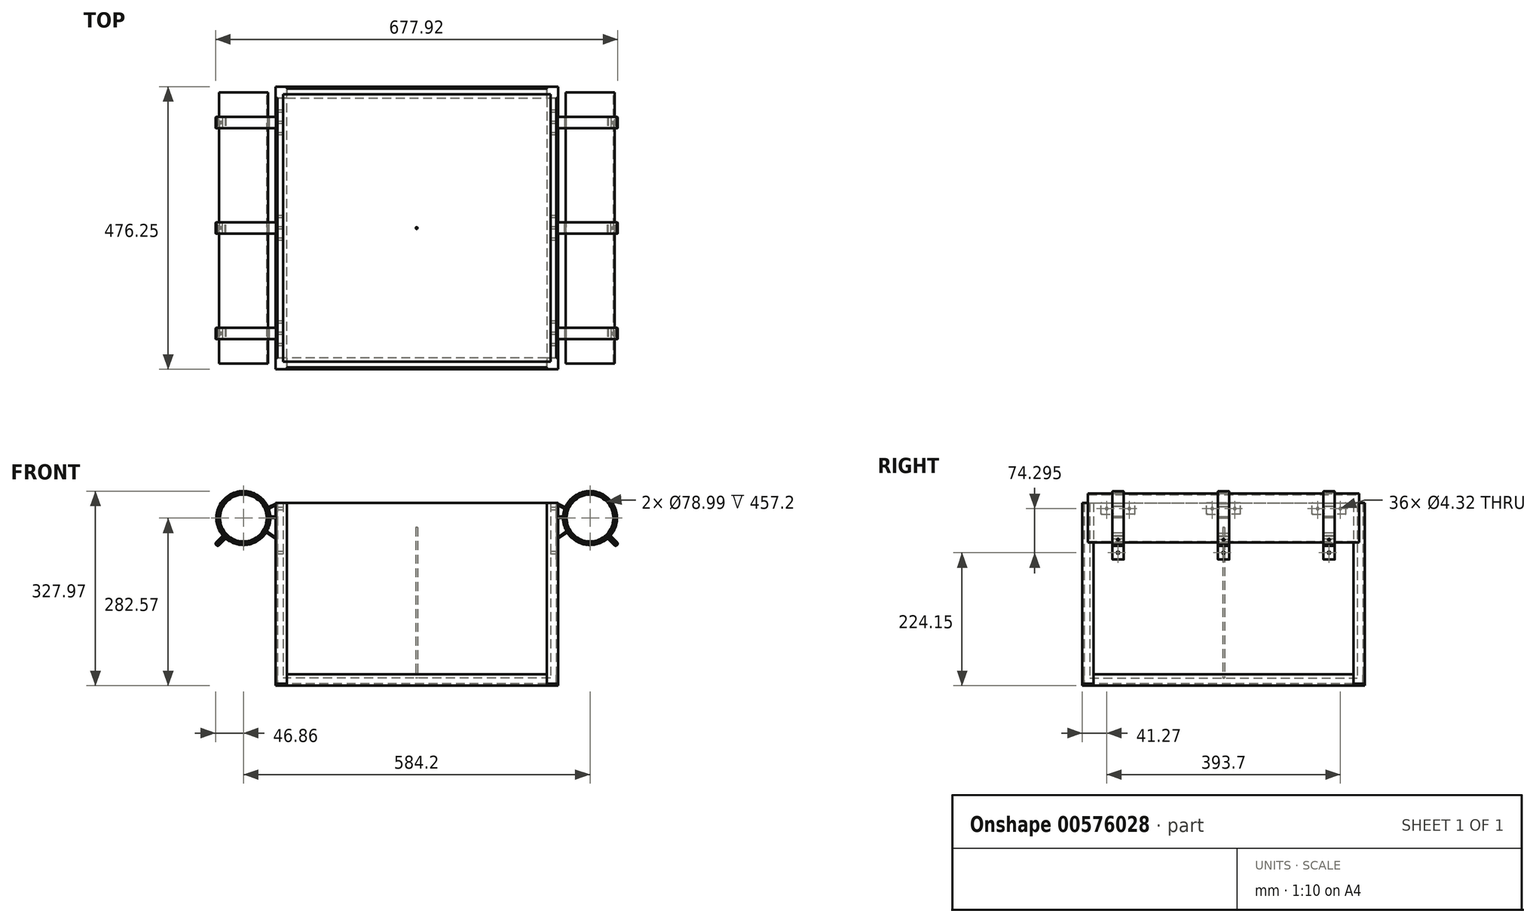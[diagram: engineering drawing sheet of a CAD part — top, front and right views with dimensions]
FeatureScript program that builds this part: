
annotation { "Feature Type Name" : "Feature", "Feature Type Description" : "" }
export const myFeature = defineFeature(function(context is Context, id is Id, definition is map)
    precondition{}
    {
        {
            var Q0;
            Q0=qCreatedBy(makeId("Top.planeOp"),FACE);
            var sketch = newSketch(context, id + "F0", { "sketchPlane" : qUnion([Q0])});
            skLineSegment(sketch, "E0.bottom", {"start": v(234.95, -234.95) * mm, "end": v(-234.95, -234.95) * mm});
            skLineSegment(sketch, "E0.top", {"start": v(234.95, 234.95) * mm, "end": v(-234.95, 234.95) * mm});
            skLineSegment(sketch, "E0.left", {"start": v(234.95, -234.95) * mm, "end": v(234.95, 234.95) * mm});
            skLineSegment(sketch, "E0.right", {"start": v(-234.95, -234.95) * mm, "end": v(-234.95, 234.95) * mm});
            skPoint(sketch, "E0.middle", {"position": v(0, 0) * mm});
            skLineSegment(sketch, "E1", {"start": v(-234.95, 238.13) * mm, "end": v(-238.13, 238.13) * mm});
            skLineSegment(sketch, "E2", {"start": v(-238.13, 238.13) * mm, "end": v(-238.13, 219.08) * mm});
            skLineSegment(sketch, "E3", {"start": v(-238.13, 219.08) * mm, "end": v(-234.95, 219.08) * mm});
            skLineSegment(sketch, "E4", {"start": v(-238.13, 238.13) * mm, "end": v(-219.08, 238.13) * mm});
            skLineSegment(sketch, "E5", {"start": v(-219.08, 238.13) * mm, "end": v(-219.08, 234.95) * mm});
            skLineSegment(sketch, "E6.1.0", {"start": v(-238.13, -238.13) * mm, "end": v(-238.13, -219.08) * mm});
            skLineSegment(sketch, "E6.1.1", {"start": v(-238.13, -238.13) * mm, "end": v(-219.08, -238.13) * mm});
            skLineSegment(sketch, "E6.1.2", {"start": v(-219.08, -238.13) * mm, "end": v(-219.08, -234.95) * mm});
            skLineSegment(sketch, "E6.1.3", {"start": v(-238.13, -219.08) * mm, "end": v(-234.95, -219.08) * mm});
            skLineSegment(sketch, "E6.1.4", {"start": v(-238.13, -234.95) * mm, "end": v(-238.13, -238.13) * mm});
            skLineSegment(sketch, "E6.2.0", {"start": v(238.13, -238.13) * mm, "end": v(219.08, -238.13) * mm});
            skLineSegment(sketch, "E6.2.1", {"start": v(238.13, -238.13) * mm, "end": v(238.13, -219.08) * mm});
            skLineSegment(sketch, "E6.2.2", {"start": v(238.13, -219.08) * mm, "end": v(234.95, -219.08) * mm});
            skLineSegment(sketch, "E6.2.3", {"start": v(219.08, -238.13) * mm, "end": v(219.08, -234.95) * mm});
            skLineSegment(sketch, "E6.2.4", {"start": v(234.95, -238.13) * mm, "end": v(238.13, -238.13) * mm});
            skLineSegment(sketch, "E6.3.0", {"start": v(238.13, 238.13) * mm, "end": v(238.13, 219.08) * mm});
            skLineSegment(sketch, "E6.3.1", {"start": v(238.13, 238.13) * mm, "end": v(219.08, 238.13) * mm});
            skLineSegment(sketch, "E6.3.2", {"start": v(219.08, 238.13) * mm, "end": v(219.08, 234.95) * mm});
            skLineSegment(sketch, "E6.3.3", {"start": v(238.13, 219.08) * mm, "end": v(234.95, 219.08) * mm});
            skLineSegment(sketch, "E6.3.4", {"start": v(238.13, 234.95) * mm, "end": v(238.13, 238.13) * mm});
            skLineSegment(sketch, "E7.0", {"start": v(225.43, 225.43) * mm, "end": v(-225.42, 225.42) * mm});
            skLineSegment(sketch, "E7.1", {"start": v(225.43, -225.42) * mm, "end": v(225.43, 225.42) * mm});
            skLineSegment(sketch, "E7.2", {"start": v(225.43, -225.42) * mm, "end": v(-225.43, -225.43) * mm});
            skLineSegment(sketch, "E7.3", {"start": v(-225.43, -225.43) * mm, "end": v(-225.42, 225.42) * mm});
            skSolve(sketch);
        }
        {
            var Q0;
            Q0=qSketchRegion(id+"F0",true);
            extrude(context, id + "F1", {"entities" : qUnion([Q0]), "depth" : 304.8 * mm, "offsetDistance" : 25.4 * mm});
        }
        {
            var Q0;
            Q0=makeQuery(id+"F0.imprint","IMPRINT",FACE,{"disambiguationData":[TD([[makeQuery(id+"F0.imprint","IMPRINT",EDGE,{"derivedFrom":sQuery(id+"F0.wireOp",EDGE,"E7.0")}),1.0]])]});
            extrude(context, id + "F2", {"entities" : qUnion([Q0]), "operationType" : NewBodyOperationType.ADD, "depth" : 9.52 * mm, "offsetDistance" : 25.4 * mm});
        }
        {
            var Q0;
            Q0=makeQuery(id+"F1.opExtrude","SWEPT_FACE",FACE,{"disambiguationData":[OSD([sQuery(id+"F0.wireOp",EDGE,"E0.right")])]});
            var sketch = newSketch(context, id + "F3", { "sketchPlane" : qUnion([Q0])});
            skLineSegment(sketch, "E8", {"start": v(0, 304.8) * mm, "end": v(0, 297.18) * mm});
            skLineSegment(sketch, "E9", {"start": v(0, 304.8) * mm, "end": v(-177.8, 304.8) * mm});
            skLineSegment(sketch, "E10", {"start": v(-177.8, 304.8) * mm, "end": v(-177.8, 297.18) * mm});
            skLineSegment(sketch, "E11", {"start": v(0, 297.18) * mm, "end": v(0, 220.98) * mm});
            skLineSegment(sketch, "E12", {"start": v(-177.8, 297.18) * mm, "end": v(-177.8, 220.98) * mm});
            skLineSegment(sketch, "E13.MirrorCS", {"start": v(177.8, 304.8) * mm, "end": v(177.8, 297.18) * mm});
            skLineSegment(sketch, "E14.MirrorCS", {"start": v(177.8, 297.18) * mm, "end": v(177.8, 220.98) * mm});
            skLineSegment(sketch, "E15.MirrorCS", {"start": v(0, 304.8) * mm, "end": v(177.8, 304.8) * mm});
            skLineSegment(sketch, "E16", {"start": v(-177.8, 304.8) * mm, "end": v(-177.8, 295.28) * mm});
            skLineSegment(sketch, "E17", {"start": v(-177.8, 295.28) * mm, "end": v(-158.75, 295.28) * mm});
            skLineSegment(sketch, "E18.MirrorCS", {"start": v(-177.8, 295.28) * mm, "end": v(-196.85, 295.28) * mm});
            skLineSegment(sketch, "E19", {"start": v(-88.9, 304.8) * mm, "end": v(-88.9, 246.4) * mm});
            skLineSegment(sketch, "E20.MirrorCS", {"start": v(0, 304.8) * mm, "end": v(0, 295.28) * mm});
            skLineSegment(sketch, "E21.MirrorCS", {"start": v(0, 295.28) * mm, "end": v(19.05, 295.28) * mm});
            skLineSegment(sketch, "E22.MirrorCS", {"start": v(0, 295.28) * mm, "end": v(-19.05, 295.28) * mm});
            skLineSegment(sketch, "E23.MirrorCS", {"start": v(177.8, 304.8) * mm, "end": v(177.8, 295.28) * mm});
            skLineSegment(sketch, "E24.MirrorCS", {"start": v(177.8, 295.28) * mm, "end": v(196.85, 295.28) * mm});
            skLineSegment(sketch, "E25.MirrorCS", {"start": v(177.8, 295.28) * mm, "end": v(158.75, 295.28) * mm});
            skSolve(sketch);
        }
        {
            var Q0;
            Q0=sQuery(id+"F3.wireOp",VERTEX,"E11.end");
            var Q1;
            Q1=sQuery(id+"F3.wireOp",VERTEX,"E14.MirrorCS.end");
            var Q2;
            Q2=sQuery(id+"F3.wireOp",VERTEX,"E17.end");
            var Q3;
            Q3=sQuery(id+"F3.wireOp",VERTEX,"E18.MirrorCS.end");
            var Q4;
            Q4=sQuery(id+"F3.wireOp",VERTEX,"E22.MirrorCS.end");
            var Q5;
            Q5=sQuery(id+"F3.wireOp",VERTEX,"E21.MirrorCS.end");
            var Q6;
            Q6=sQuery(id+"F3.wireOp",VERTEX,"E12.end");
            var Q7;
            Q7=sQuery(id+"F3.wireOp",VERTEX,"E24.MirrorCS.end");
            var Q8;
            Q8=sQuery(id+"F3.wireOp",VERTEX,"E25.MirrorCS.end");
            var Q9;
            Q9=makeQuery(id+"F1.opExtrude","SWEPT_BODY",BODY,{"disambiguationData":[OSD([sQuery(id+"F0.wireOp",EDGE,"E0.bottom"),sQuery(id+"F0.wireOp",EDGE,"E0.top"),sQuery(id+"F0.wireOp",EDGE,"E0.left"),sQuery(id+"F0.wireOp",EDGE,"E0.right"),sQuery(id+"F0.wireOp",EDGE,"E2"),sQuery(id+"F0.wireOp",EDGE,"E3"),sQuery(id+"F0.wireOp",EDGE,"E4"),sQuery(id+"F0.wireOp",EDGE,"E5"),sQuery(id+"F0.wireOp",EDGE,"E6.1.0"),sQuery(id+"F0.wireOp",EDGE,"E6.1.1"),sQuery(id+"F0.wireOp",EDGE,"E6.1.2"),sQuery(id+"F0.wireOp",EDGE,"E6.1.3"),sQuery(id+"F0.wireOp",EDGE,"E6.1.4"),sQuery(id+"F0.wireOp",EDGE,"E6.2.0"),sQuery(id+"F0.wireOp",EDGE,"E6.2.1"),sQuery(id+"F0.wireOp",EDGE,"E6.2.2"),sQuery(id+"F0.wireOp",EDGE,"E6.2.3"),sQuery(id+"F0.wireOp",EDGE,"E6.2.4"),sQuery(id+"F0.wireOp",EDGE,"E6.3.0"),sQuery(id+"F0.wireOp",EDGE,"E6.3.1"),sQuery(id+"F0.wireOp",EDGE,"E6.3.2"),sQuery(id+"F0.wireOp",EDGE,"E6.3.3"),sQuery(id+"F0.wireOp",EDGE,"E6.3.4"),sQuery(id+"F0.wireOp",EDGE,"E7.0"),sQuery(id+"F0.wireOp",EDGE,"E7.1"),sQuery(id+"F0.wireOp",EDGE,"E7.2"),sQuery(id+"F0.wireOp",EDGE,"E7.3")])]});
            hole(context, id + "F4", {"style" : HoleStyle.SIMPLE, "endStyle" : HoleEndStyle.BLIND, "standardTappedOrClearance" : lookupTablePath({ "standard" : "ANSI", "fit" : "Close", "size" : "#8", "type" : "Clearance" }), "standardBlindInLast" : lookupTablePath({ "fit" : "Close", "standard" : "ANSI", "size" : "#8", "type" : "Clearance" }), "holeDiameter" : 4.32 * mm, "holeDepth" : 762 * mm, "isTappedThrough" : true, "tappedDepth" : 12.7 * mm, "tapClearance" : 3, "locations" : qUnion([Q0, Q1, Q2, Q3, Q4, Q5, Q6, Q7, Q8]), "scope" : qUnion([Q9]), "majorDiameter" : 6.35 * mm});
        }
        {
            var Q0;
            Q0=makeQuery(id+"F1.opExtrude","SWEPT_FACE",FACE,{"disambiguationData":[OSD([sQuery(id+"F0.wireOp",EDGE,"E6.1.2")])]});
            var sketch = newSketch(context, id + "F5", { "sketchPlane" : qUnion([Q0])});
            skLineSegment(sketch, "E26", {"start": v(-238.12, -3.17) * mm, "end": v(-238.12, 15.87) * mm});
            skLineSegment(sketch, "E27", {"start": v(-238.12, 15.87) * mm, "end": v(-234.95, 15.87) * mm});
            skLineSegment(sketch, "E28", {"start": v(-234.95, 15.87) * mm, "end": v(-234.95, 0) * mm});
            skLineSegment(sketch, "E29", {"start": v(-234.95, 0) * mm, "end": v(-219.07, 0) * mm});
            skLineSegment(sketch, "E30", {"start": v(-219.07, 0) * mm, "end": v(-219.07, -3.17) * mm});
            skLineSegment(sketch, "E31", {"start": v(-219.07, -3.17) * mm, "end": v(-238.12, -3.17) * mm});
            skSolve(sketch);
        }
        {
            var Q0;
            Q0=qSketchRegion(id+"F5",true);
            var Q1;
            Q1=makeQuery(id+"F1.opExtrude","SWEPT_FACE",FACE,{"disambiguationData":[OSD([sQuery(id+"F0.wireOp",EDGE,"E6.2.3")])]});
            extrude(context, id + "F6", {"entities" : qUnion([Q0]), "endBound" : BoundingType.UP_TO_SURFACE, "depth" : 25.4 * mm, "endBoundEntityFace" : qUnion([Q1]), "offsetDistance" : 25.4 * mm});
        }
        {
            var Q0;
            Q0=makeQuery(id+"F2.opExtrude","CAP_FACE",FACE,{"disambiguationData":[OSD([sQuery(id+"F0.wireOp",EDGE,"E7.0"),sQuery(id+"F0.wireOp",EDGE,"E7.1"),sQuery(id+"F0.wireOp",EDGE,"E7.2"),sQuery(id+"F0.wireOp",EDGE,"E7.3")])],"isStart":false});
            var sketch = newSketch(context, id + "F7", { "sketchPlane" : qUnion([Q0])});
            skCircle(sketch, "E32", {"center": v(0, 0) * mm, "radius": 1.59 * mm});
            skSolve(sketch);
        }
        {
            var Q0;
            Q0=qSketchRegion(id+"F7",true);
            extrude(context, id + "F8", {"entities" : qUnion([Q0]), "operationType" : NewBodyOperationType.ADD, "depth" : 254 * mm, "offsetDistance" : 25.4 * mm});
        }
        {
            var Q0;
            Q0=makeQuery(id+"F6.opExtrude","SWEPT_BODY",BODY,{"disambiguationData":[OSD([sQuery(id+"F5.wireOp",EDGE,"E26"),sQuery(id+"F5.wireOp",EDGE,"E27"),sQuery(id+"F5.wireOp",EDGE,"E28"),sQuery(id+"F5.wireOp",EDGE,"E29"),sQuery(id+"F5.wireOp",EDGE,"E30"),sQuery(id+"F5.wireOp",EDGE,"E31")])]});
            var Q1;
            Q1=makeQuery(id+"F8.opExtrude","SWEPT_FACE",FACE,{"disambiguationData":[OSD([sQuery(id+"F7.wireOp",EDGE,"E32")])]});
            circularPattern(context, id + "F9", {"entities" : qUnion([Q0]), "axis" : qUnion([Q1]), "angle" : 360 * degree, "instanceCount" : 4, "equalSpace" : true});
        }
        {
            var Q0;
            Q0=qCreatedBy(makeId("Front.planeOp"),FACE);
            var sketch = newSketch(context, id + "F10", { "sketchPlane" : qUnion([Q0])});
            skLineSegment(sketch, "E33", {"start": v(0, 0) * mm, "end": v(0, 279.4) * mm});
            skLineSegment(sketch, "E34", {"start": v(0, 279.4) * mm, "end": v(238.13, 279.4) * mm});
            skCircle(sketch, "E35", {"center": v(292.1, 279.4) * mm, "radius": 41.28 * mm});
            skCircle(sketch, "E36", {"center": v(292.1, 279.4) * mm, "radius": 39.5 * mm});
            skLineSegment(sketch, "E37", {"start": v(292.1, 279.4) * mm, "end": v(250.83, 279.4) * mm});
            skLineSegment(sketch, "E38", {"start": v(250.83, 279.4) * mm, "end": v(238.13, 279.4) * mm});
            skSolve(sketch);
        }
        {
            var Q0;
            Q0 = qSketchRegion(id + "F10", true);
            extrude(context, id + "F11", {"entities" : qUnion([Q0]), "endBound" : BoundingType.SYMMETRIC, "depth" : 457.2 * mm, "offsetDistance" : 25.4 * mm});
        }
        {
            var Q0;
            Q0=qCreatedBy(makeId("Front.planeOp"),FACE);
            var sketch = newSketch(context, id + "F12", { "sketchPlane" : qUnion([Q0])});
            skLineSegment(sketch, "E39", {"start": v(0, 0) * mm, "end": v(0, 40.83) * mm});
            skLineSegment(sketch, "E40", {"start": v(248.33, 298.8) * mm, "end": v(237.5, 303.6) * mm});
            skLineSegment(sketch, "E41", {"start": v(237.5, 209.55) * mm, "end": v(234.95, 209.55) * mm});
            skLineSegment(sketch, "E42", {"start": v(251.7, 253.53) * mm, "end": v(238.58, 244.41) * mm});
            skArc(sketch, "E43.0", {"start": v(322.94, 249.64) * mm, "mid": v(261.8, 309.7) * mm, "end": v(321.86, 248.56) * mm});
            skArc(sketch, "E44.0", {"start": v(246.75, 277.28) * mm, "mid": v(248.16, 267.95) * mm, "end": v(251.48, 259.12) * mm});
            skLineSegment(sketch, "E45", {"start": v(244.2, 279.7) * mm, "end": v(240.03, 279.7) * mm});
            skLineSegment(sketch, "E46.0", {"start": v(244.46, 282.24) * mm, "end": v(240.03, 282.24) * mm});
            skLineSegment(sketch, "E47.trimOffspring", {"start": v(237.5, 296.8) * mm, "end": v(237.5, 284.78) * mm});
            skLineSegment(sketch, "E48.trimOffspring", {"start": v(247.46, 296.1) * mm, "end": v(241.11, 299.1) * mm});
            skLineSegment(sketch, "E49.trimOffspring", {"start": v(237.5, 277.16) * mm, "end": v(237.5, 251.6) * mm});
            skArc(sketch, "E50.trimOffspring", {"start": v(255.22, 252.93) * mm, "mid": v(285.65, 234.46) * mm, "end": v(320.05, 243.62) * mm});
            skLineSegment(sketch, "E51.trimOffspring", {"start": v(250.66, 255.9) * mm, "end": v(241.48, 249.52) * mm});
            skLineSegment(sketch, "E52.trimOffspring", {"start": v(237.5, 242.33) * mm, "end": v(237.5, 209.55) * mm});
            skArc(sketch, "E53.trimOffspring", {"start": v(248.8, 293.05) * mm, "mid": v(247.68, 288.82) * mm, "end": v(246.98, 284.5) * mm});
            skLineSegment(sketch, "E54", {"start": v(292.1, 279.4) * mm, "end": v(292.1, 252.05) * mm});
            skLineSegment(sketch, "E55", {"start": v(292.1, 279.4) * mm, "end": v(324.2, 247.3) * mm});
            skLineSegment(sketch, "E56", {"start": v(324.2, 247.3) * mm, "end": v(337.67, 233.83) * mm});
            skLineSegment(sketch, "E57.0", {"start": v(323.66, 246.76) * mm, "end": v(337.14, 233.28) * mm});
            skLineSegment(sketch, "E58.0", {"start": v(324.74, 247.84) * mm, "end": v(338.22, 234.36) * mm});
            skArc(sketch, "E59.trimOffspring", {"start": v(327.88, 251.45) * mm, "mid": v(316.48, 317.7) * mm, "end": v(251.62, 299.97) * mm});
            skLineSegment(sketch, "E60", {"start": v(323.66, 246.76) * mm, "end": v(321.86, 248.56) * mm});
            skLineSegment(sketch, "E61", {"start": v(324.74, 247.84) * mm, "end": v(322.94, 249.64) * mm});
            skLineSegment(sketch, "E62", {"start": v(337.14, 233.28) * mm, "end": v(337.14, 233.28) * mm});
            skLineSegment(sketch, "E63", {"start": v(333.55, 233.28) * mm, "end": v(323.41, 243.42) * mm});
            skLineSegment(sketch, "E64.MirrorCS", {"start": v(338.22, 237.95) * mm, "end": v(328.08, 248.09) * mm});
            skLineSegment(sketch, "E65.MirrorCS", {"start": v(338.22, 234.36) * mm, "end": v(338.22, 234.36) * mm});
            skPoint(sketch, "E66.visualSharp", {"position": v(250.6, 297.8) * mm});
            skArc(sketch, "E66.filletArc", {"start": v(248.33, 298.8) * mm, "mid": v(250.21, 298.73) * mm, "end": v(251.62, 299.97) * mm});
            skPoint(sketch, "E67.visualSharp", {"position": v(249.51, 295.14) * mm});
            skArc(sketch, "E67.filletArc", {"start": v(248.8, 293.05) * mm, "mid": v(248.7, 294.83) * mm, "end": v(247.46, 296.1) * mm});
            skPoint(sketch, "E68.visualSharp", {"position": v(237.5, 300.8) * mm});
            skArc(sketch, "E68.filletArc", {"start": v(241.11, 299.1) * mm, "mid": v(238.67, 298.94) * mm, "end": v(237.5, 296.8) * mm});
            skPoint(sketch, "E69.visualSharp", {"position": v(246.79, 282.24) * mm});
            skArc(sketch, "E69.filletArc", {"start": v(244.46, 282.24) * mm, "mid": v(246.15, 282.89) * mm, "end": v(246.98, 284.5) * mm});
            skPoint(sketch, "E70.visualSharp", {"position": v(237.5, 282.24) * mm});
            skArc(sketch, "E70.filletArc", {"start": v(237.5, 284.78) * mm, "mid": v(238.23, 282.99) * mm, "end": v(240.03, 282.24) * mm});
            skPoint(sketch, "E71.visualSharp", {"position": v(237.5, 279.7) * mm});
            skArc(sketch, "E71.filletArc", {"start": v(240.03, 279.7) * mm, "mid": v(238.23, 278.96) * mm, "end": v(237.5, 277.16) * mm});
            skPoint(sketch, "E72.visualSharp", {"position": v(246.7, 279.7) * mm});
            skArc(sketch, "E72.filletArc", {"start": v(246.75, 277.28) * mm, "mid": v(245.96, 279) * mm, "end": v(244.2, 279.7) * mm});
            skPoint(sketch, "E73.visualSharp", {"position": v(252.5, 257.18) * mm});
            skArc(sketch, "E73.filletArc", {"start": v(250.66, 255.9) * mm, "mid": v(251.67, 257.35) * mm, "end": v(251.48, 259.12) * mm});
            skPoint(sketch, "E74.visualSharp", {"position": v(237.5, 246.75) * mm});
            skArc(sketch, "E74.filletArc", {"start": v(237.5, 251.6) * mm, "mid": v(238.85, 249.35) * mm, "end": v(241.48, 249.52) * mm});
            skPoint(sketch, "E75.visualSharp", {"position": v(237.5, 243.65) * mm});
            skArc(sketch, "E75.filletArc", {"start": v(238.58, 244.41) * mm, "mid": v(237.78, 243.5) * mm, "end": v(237.5, 242.33) * mm});
            skPoint(sketch, "E76.visualSharp", {"position": v(253.81, 255) * mm});
            skArc(sketch, "E76.filletArc", {"start": v(255.22, 252.93) * mm, "mid": v(253.58, 253.95) * mm, "end": v(251.7, 253.53) * mm});
            skPoint(sketch, "E77.visualSharp", {"position": v(321.78, 245.05) * mm});
            skArc(sketch, "E77.filletArc", {"start": v(323.41, 243.42) * mm, "mid": v(321.77, 244.16) * mm, "end": v(320.05, 243.62) * mm});
            skPoint(sketch, "E78.visualSharp", {"position": v(326.45, 249.72) * mm});
            skArc(sketch, "E78.filletArc", {"start": v(327.88, 251.45) * mm, "mid": v(327.34, 249.73) * mm, "end": v(328.08, 248.09) * mm});
            skPoint(sketch, "E79.visualSharp", {"position": v(340.01, 236.16) * mm});
            skArc(sketch, "E79.filletArc", {"start": v(338.22, 234.36) * mm, "mid": v(338.96, 236.16) * mm, "end": v(338.22, 237.95) * mm});
            skPoint(sketch, "E80.visualSharp", {"position": v(335.34, 231.49) * mm});
            skArc(sketch, "E80.filletArc", {"start": v(333.55, 233.28) * mm, "mid": v(335.34, 232.54) * mm, "end": v(337.14, 233.28) * mm});
            skPoint(sketch, "E81.visualSharp", {"position": v(237.5, 304.8) * mm});
            skLineSegment(sketch, "E82", {"start": v(237.5, 303.6) * mm, "end": v(237.5, 304.8) * mm});
            skLineSegment(sketch, "E83", {"start": v(234.95, 304.8) * mm, "end": v(237.5, 304.8) * mm});
            skLineSegment(sketch, "E84", {"start": v(234.95, 209.55) * mm, "end": v(234.95, 304.8) * mm});
            skSolve(sketch);
        }
        {
            var Q0;
            Q0 = qSketchRegion(id + "F12", true);
            extrude(context, id + "F13", {"entities" : qUnion([Q0]), "endBound" : BoundingType.SYMMETRIC, "depth" : 19.05 * mm, "offsetDistance" : 25.4 * mm});
        }
        {
            var Q0;
            Q0=makeQuery(id+"F13.opExtrude","SWEPT_FACE",FACE,{"disambiguationData":[OSD([sQuery(id+"F12.wireOp",EDGE,"E64.MirrorCS")])]});
            var sketch = newSketch(context, id + "F14", { "sketchPlane" : qUnion([Q0])});
            skLineSegment(sketch, "E85", {"start": v(-9.53, -56.57) * mm, "end": v(9.53, -70.9) * mm});
            skLineSegment(sketch, "E86", {"start": v(9.53, -56.57) * mm, "end": v(-9.53, -70.9) * mm});
            skLineSegment(sketch, "E87", {"start": v(-9.53, -70.9) * mm, "end": v(0, -63.73) * mm});
            skLineSegment(sketch, "E88", {"start": v(0, -63.73) * mm, "end": v(0, -59.85) * mm});
            skSolve(sketch);
        }
        {
            var Q0;
            Q0=sQuery(id+"F14.wireOp",VERTEX,"E88.start");
            var Q1;
            Q1=makeQuery(id+"F13.opExtrude","SWEPT_BODY",BODY,{"disambiguationData":[OSD([sQuery(id+"F12.wireOp",EDGE,"E40"),sQuery(id+"F12.wireOp",EDGE,"XVp6BJce-8Tfc-asBP-cGqg-N5JEgT9na927"),sQuery(id+"F12.wireOp",EDGE,"cfrEHy57-AOKR-8SEr-zHKb-8GyFvIi9nsPC"),sQuery(id+"F12.wireOp",EDGE,"E41"),sQuery(id+"F12.wireOp",EDGE,"E42"),sQuery(id+"F12.wireOp",EDGE,"E43.0"),sQuery(id+"F12.wireOp",EDGE,"E44.0"),sQuery(id+"F12.wireOp",EDGE,"E45"),sQuery(id+"F12.wireOp",EDGE,"E46.0"),sQuery(id+"F12.wireOp",EDGE,"E47.trimOffspring"),sQuery(id+"F12.wireOp",EDGE,"E48.trimOffspring"),sQuery(id+"F12.wireOp",EDGE,"E49.trimOffspring"),sQuery(id+"F12.wireOp",EDGE,"E50.trimOffspring"),sQuery(id+"F12.wireOp",EDGE,"E51.trimOffspring"),sQuery(id+"F12.wireOp",EDGE,"E52.trimOffspring"),sQuery(id+"F12.wireOp",EDGE,"E53.trimOffspring"),sQuery(id+"F12.wireOp",EDGE,"E57.0"),sQuery(id+"F12.wireOp",EDGE,"E58.0"),sQuery(id+"F12.wireOp",EDGE,"E59.trimOffspring"),sQuery(id+"F12.wireOp",EDGE,"E60"),sQuery(id+"F12.wireOp",EDGE,"E61"),sQuery(id+"F12.wireOp",EDGE,"E63"),sQuery(id+"F12.wireOp",EDGE,"E64.MirrorCS"),sQuery(id+"F12.wireOp",EDGE,"E66.filletArc"),sQuery(id+"F12.wireOp",EDGE,"E67.filletArc"),sQuery(id+"F12.wireOp",EDGE,"E68.filletArc"),sQuery(id+"F12.wireOp",EDGE,"E69.filletArc"),sQuery(id+"F12.wireOp",EDGE,"E70.filletArc"),sQuery(id+"F12.wireOp",EDGE,"E71.filletArc"),sQuery(id+"F12.wireOp",EDGE,"E72.filletArc"),sQuery(id+"F12.wireOp",EDGE,"E73.filletArc"),sQuery(id+"F12.wireOp",EDGE,"E74.filletArc"),sQuery(id+"F12.wireOp",EDGE,"E75.filletArc"),sQuery(id+"F12.wireOp",EDGE,"E76.filletArc"),sQuery(id+"F12.wireOp",EDGE,"E77.filletArc"),sQuery(id+"F12.wireOp",EDGE,"E78.filletArc"),sQuery(id+"F12.wireOp",EDGE,"E79.filletArc"),sQuery(id+"F12.wireOp",EDGE,"E80.filletArc"),sQuery(id+"F12.wireOp",EDGE,"E81.filletArc"),sQuery(id+"F12.wireOp",EDGE,"QRnfTjK7-z6Yt-K2ef-ZXCt-E60ytMqK47gu")])]});
            hole(context, id + "F15", {"style" : HoleStyle.SIMPLE, "endStyle" : HoleEndStyle.BLIND, "standardTappedOrClearance" : lookupTablePath({ "standard" : "ANSI", "fit" : "Close", "size" : "#6", "type" : "Clearance" }), "standardBlindInLast" : lookupTablePath({ "fit" : "Close", "standard" : "ANSI", "size" : "#6", "type" : "Clearance" }), "holeDiameter" : 3.66 * mm, "majorDiameter" : 6.35 * mm, "holeDepth" : 25.4 * mm, "isTappedThrough" : true, "tappedDepth" : 12.7 * mm, "tapClearance" : 3, "locations" : qUnion([Q0]), "scope" : qUnion([Q1])});
        }
        {
            var Q0;
            Q0=makeQuery(id+"F13.opExtrude","CAP_FACE",FACE,{"disambiguationData":[OSD([sQuery(id+"F12.wireOp",EDGE,"E40"),sQuery(id+"F12.wireOp",EDGE,"E41"),sQuery(id+"F12.wireOp",EDGE,"E42"),sQuery(id+"F12.wireOp",EDGE,"E43.0"),sQuery(id+"F12.wireOp",EDGE,"E44.0"),sQuery(id+"F12.wireOp",EDGE,"E45"),sQuery(id+"F12.wireOp",EDGE,"E46.0"),sQuery(id+"F12.wireOp",EDGE,"E47.trimOffspring"),sQuery(id+"F12.wireOp",EDGE,"E48.trimOffspring"),sQuery(id+"F12.wireOp",EDGE,"E49.trimOffspring"),sQuery(id+"F12.wireOp",EDGE,"E50.trimOffspring"),sQuery(id+"F12.wireOp",EDGE,"E51.trimOffspring"),sQuery(id+"F12.wireOp",EDGE,"E52.trimOffspring"),sQuery(id+"F12.wireOp",EDGE,"E53.trimOffspring"),sQuery(id+"F12.wireOp",EDGE,"E57.0"),sQuery(id+"F12.wireOp",EDGE,"E58.0"),sQuery(id+"F12.wireOp",EDGE,"E59.trimOffspring"),sQuery(id+"F12.wireOp",EDGE,"E60"),sQuery(id+"F12.wireOp",EDGE,"E61"),sQuery(id+"F12.wireOp",EDGE,"E63"),sQuery(id+"F12.wireOp",EDGE,"E64.MirrorCS"),sQuery(id+"F12.wireOp",EDGE,"E66.filletArc"),sQuery(id+"F12.wireOp",EDGE,"E67.filletArc"),sQuery(id+"F12.wireOp",EDGE,"E68.filletArc"),sQuery(id+"F12.wireOp",EDGE,"E69.filletArc"),sQuery(id+"F12.wireOp",EDGE,"E70.filletArc"),sQuery(id+"F12.wireOp",EDGE,"E71.filletArc"),sQuery(id+"F12.wireOp",EDGE,"E72.filletArc"),sQuery(id+"F12.wireOp",EDGE,"E73.filletArc"),sQuery(id+"F12.wireOp",EDGE,"E74.filletArc"),sQuery(id+"F12.wireOp",EDGE,"E75.filletArc"),sQuery(id+"F12.wireOp",EDGE,"E76.filletArc"),sQuery(id+"F12.wireOp",EDGE,"E77.filletArc"),sQuery(id+"F12.wireOp",EDGE,"E78.filletArc"),sQuery(id+"F12.wireOp",EDGE,"E79.filletArc"),sQuery(id+"F12.wireOp",EDGE,"E80.filletArc"),sQuery(id+"F12.wireOp",EDGE,"E82"),sQuery(id+"F12.wireOp",EDGE,"E83"),sQuery(id+"F12.wireOp",EDGE,"E84")])],"isStart":false});
            var sketch = newSketch(context, id + "F16", { "sketchPlane" : qUnion([Q0])});
            skLineSegment(sketch, "E89", {"start": v(234.95, 304.8) * mm, "end": v(237.5, 304.8) * mm});
            skLineSegment(sketch, "E90", {"start": v(237.5, 304.8) * mm, "end": v(237.5, 285.75) * mm});
            skLineSegment(sketch, "E91", {"start": v(237.5, 285.75) * mm, "end": v(234.95, 285.75) * mm});
            skLineSegment(sketch, "E92", {"start": v(234.95, 285.75) * mm, "end": v(234.95, 304.8) * mm});
            skSolve(sketch);
        }
        {
            var Q0;
            Q0 = qSketchRegion(id + "F16", true);
            extrude(context, id + "F17", {"entities" : qUnion([Q0]), "depth" : 19.05 * mm, "offsetDistance" : 25.4 * mm});
        }
        {
            var Q0;
            Q0=makeQuery(id+"F17.opExtrude","SWEPT_BODY",BODY,{"disambiguationData":[OSD([sQuery(id+"F16.wireOp",EDGE,"E89"),sQuery(id+"F16.wireOp",EDGE,"E90"),sQuery(id+"F16.wireOp",EDGE,"E91"),sQuery(id+"F16.wireOp",EDGE,"E92")])]});
            var Q1;
            Q1=qCreatedBy(makeId("Front.planeOp"),FACE);
            mirror(context, id + "F18", {"entities" : qUnion([Q0]), "mirrorPlane" : qUnion([Q1])});
        }
        {
            var Q0;
            Q0=makeQuery(id+"F18.opPattern","COPY",BODY,{"derivedFrom":makeQuery(id+"F17.opExtrude","SWEPT_BODY",BODY,{"disambiguationData":[OSD([sQuery(id+"F16.wireOp",EDGE,"E89"),sQuery(id+"F16.wireOp",EDGE,"E90"),sQuery(id+"F16.wireOp",EDGE,"E91"),sQuery(id+"F16.wireOp",EDGE,"E92")])]}),"instanceName":"1"});
            var Q1;
            Q1=makeQuery(id+"F17.opExtrude","SWEPT_BODY",BODY,{"disambiguationData":[OSD([sQuery(id+"F16.wireOp",EDGE,"E89"),sQuery(id+"F16.wireOp",EDGE,"E90"),sQuery(id+"F16.wireOp",EDGE,"E91"),sQuery(id+"F16.wireOp",EDGE,"E92")])]});
            var Q2;
            Q2=makeQuery(id+"F13.opExtrude","SWEPT_BODY",BODY,{"disambiguationData":[OSD([sQuery(id+"F12.wireOp",EDGE,"E40"),sQuery(id+"F12.wireOp",EDGE,"E41"),sQuery(id+"F12.wireOp",EDGE,"E42"),sQuery(id+"F12.wireOp",EDGE,"E43.0"),sQuery(id+"F12.wireOp",EDGE,"E44.0"),sQuery(id+"F12.wireOp",EDGE,"E45"),sQuery(id+"F12.wireOp",EDGE,"E46.0"),sQuery(id+"F12.wireOp",EDGE,"E47.trimOffspring"),sQuery(id+"F12.wireOp",EDGE,"E48.trimOffspring"),sQuery(id+"F12.wireOp",EDGE,"E49.trimOffspring"),sQuery(id+"F12.wireOp",EDGE,"E50.trimOffspring"),sQuery(id+"F12.wireOp",EDGE,"E51.trimOffspring"),sQuery(id+"F12.wireOp",EDGE,"E52.trimOffspring"),sQuery(id+"F12.wireOp",EDGE,"E53.trimOffspring"),sQuery(id+"F12.wireOp",EDGE,"E57.0"),sQuery(id+"F12.wireOp",EDGE,"E58.0"),sQuery(id+"F12.wireOp",EDGE,"E59.trimOffspring"),sQuery(id+"F12.wireOp",EDGE,"E60"),sQuery(id+"F12.wireOp",EDGE,"E61"),sQuery(id+"F12.wireOp",EDGE,"E63"),sQuery(id+"F12.wireOp",EDGE,"E64.MirrorCS"),sQuery(id+"F12.wireOp",EDGE,"E66.filletArc"),sQuery(id+"F12.wireOp",EDGE,"E67.filletArc"),sQuery(id+"F12.wireOp",EDGE,"E68.filletArc"),sQuery(id+"F12.wireOp",EDGE,"E69.filletArc"),sQuery(id+"F12.wireOp",EDGE,"E70.filletArc"),sQuery(id+"F12.wireOp",EDGE,"E71.filletArc"),sQuery(id+"F12.wireOp",EDGE,"E72.filletArc"),sQuery(id+"F12.wireOp",EDGE,"E73.filletArc"),sQuery(id+"F12.wireOp",EDGE,"E74.filletArc"),sQuery(id+"F12.wireOp",EDGE,"E75.filletArc"),sQuery(id+"F12.wireOp",EDGE,"E76.filletArc"),sQuery(id+"F12.wireOp",EDGE,"E77.filletArc"),sQuery(id+"F12.wireOp",EDGE,"E78.filletArc"),sQuery(id+"F12.wireOp",EDGE,"E79.filletArc"),sQuery(id+"F12.wireOp",EDGE,"E80.filletArc"),sQuery(id+"F12.wireOp",EDGE,"E82"),sQuery(id+"F12.wireOp",EDGE,"E83"),sQuery(id+"F12.wireOp",EDGE,"E84")])]});
            booleanBodies(context, id + "F19", {"operationType" : BooleanOperationType.UNION, "tools" : qUnion([Q0, Q1, Q2])});
        }
        {
            var Q0;
            {var subQ0=makeQuery(id+"F17.opExtrude","SWEPT_FACE",FACE,{"disambiguationData":[OSD([sQuery(id+"F16.wireOp",EDGE,"E90")])]});Q0=makeQuery(id+"F19.opBoolean","MERGE",FACE,{"derivedFrom":[makeQuery(id+"F13.opExtrude","SWEPT_FACE",FACE,{"disambiguationData":[OSD([sQuery(id+"F12.wireOp",EDGE,"E47.trimOffspring")])]}),makeQuery(id+"F13.opExtrude","SWEPT_FACE",FACE,{"disambiguationData":[OSD([sQuery(id+"F12.wireOp",EDGE,"E82")])]}),subQ0,makeQuery(id+"F18.opPattern","COPY",FACE,{"derivedFrom":subQ0,"instanceName":"1"})]});}
            var sketch = newSketch(context, id + "F20", { "sketchPlane" : qUnion([Q0])});
            skLineSegment(sketch, "E93", {"start": v(-28.58, 304.8) * mm, "end": v(28.58, 304.8) * mm});
            skLineSegment(sketch, "E94", {"start": v(-28.58, 304.8) * mm, "end": v(-19.05, 304.8) * mm});
            skLineSegment(sketch, "E95", {"start": v(-19.05, 304.8) * mm, "end": v(-19.05, 295.28) * mm});
            skLineSegment(sketch, "E96", {"start": v(0, 304.8) * mm, "end": v(0, 288.55) * mm});
            skLineSegment(sketch, "E97.MirrorCS", {"start": v(28.58, 304.8) * mm, "end": v(19.05, 304.8) * mm});
            skLineSegment(sketch, "E98.MirrorCS", {"start": v(19.05, 304.8) * mm, "end": v(19.05, 295.28) * mm});
            skSolve(sketch);
        }
        {
            var Q0;
            Q0=sQuery(id+"F20.wireOp",VERTEX,"E98.MirrorCS.end");
            var Q1;
            Q1=sQuery(id+"F20.wireOp",VERTEX,"E95.end");
            var Q2;
            Q2=makeQuery(id+"F18.opPattern","COPY",BODY,{"derivedFrom":makeQuery(id+"F17.opExtrude","SWEPT_BODY",BODY,{"disambiguationData":[OSD([sQuery(id+"F16.wireOp",EDGE,"E89"),sQuery(id+"F16.wireOp",EDGE,"E90"),sQuery(id+"F16.wireOp",EDGE,"E91"),sQuery(id+"F16.wireOp",EDGE,"E92")])]}),"instanceName":"1"});
            hole(context, id + "F21", {"style" : HoleStyle.SIMPLE, "endStyle" : HoleEndStyle.THROUGH, "standardTappedOrClearance" : lookupTablePath({ "standard" : "ANSI", "fit" : "Close", "size" : "#8", "type" : "Clearance" }), "standardBlindInLast" : lookupTablePath({ "fit" : "Close", "standard" : "ANSI", "size" : "#8", "type" : "Clearance" }), "holeDiameter" : 4.32 * mm, "majorDiameter" : 6.35 * mm, "isTappedThrough" : true, "tappedDepth" : 12.7 * mm, "tapClearance" : 3, "locations" : qUnion([Q0, Q1]), "scope" : qUnion([Q2])});
        }
        {
            var Q0;
            Q0=makeQuery(id+"F13.opExtrude","SWEPT_FACE",FACE,{"disambiguationData":[OSD([sQuery(id+"F12.wireOp",EDGE,"E52.trimOffspring")])]});
            var sketch = newSketch(context, id + "F22", { "sketchPlane" : qUnion([Q0])});
            skLineSegment(sketch, "E99", {"start": v(0, 209.55) * mm, "end": v(0, 220.98) * mm});
            skSolve(sketch);
        }
        {
            var Q0;
            Q0=sQuery(id+"F22.wireOp",VERTEX,"E99.end");
            var Q1;
            Q1=makeQuery(id+"F18.opPattern","COPY",BODY,{"derivedFrom":makeQuery(id+"F17.opExtrude","SWEPT_BODY",BODY,{"disambiguationData":[OSD([sQuery(id+"F16.wireOp",EDGE,"E89"),sQuery(id+"F16.wireOp",EDGE,"E90"),sQuery(id+"F16.wireOp",EDGE,"E91"),sQuery(id+"F16.wireOp",EDGE,"E92")])]}),"instanceName":"1"});
            hole(context, id + "F23", {"style" : HoleStyle.SIMPLE, "endStyle" : HoleEndStyle.THROUGH, "standardTappedOrClearance" : lookupTablePath({ "standard" : "ANSI", "fit" : "Close", "size" : "#8", "type" : "Clearance" }), "standardBlindInLast" : lookupTablePath({ "fit" : "Close", "standard" : "ANSI", "size" : "#8", "type" : "Clearance" }), "holeDiameter" : 4.32 * mm, "majorDiameter" : 6.35 * mm, "isTappedThrough" : true, "tappedDepth" : 12.7 * mm, "tapClearance" : 3, "locations" : qUnion([Q0]), "scope" : qUnion([Q1])});
        }
        {
            var Q0;
            Q0=makeQuery(id+"F13.opExtrude","CAP_EDGE",EDGE,{"disambiguationData":[OSD([sQuery(id+"F12.wireOp",EDGE,"E59.trimOffspring")])],"isStart":false});
            var Q1;
            Q1=makeQuery(id+"F13.opExtrude","CAP_EDGE",EDGE,{"disambiguationData":[OSD([sQuery(id+"F12.wireOp",EDGE,"E59.trimOffspring")])],"isStart":true});
            var Q2;
            Q2=makeQuery(id+"F17.opExtrude","CAP_EDGE",EDGE,{"disambiguationData":[OSD([sQuery(id+"F16.wireOp",EDGE,"E90")])],"isStart":false});
            var Q3;
            Q3=makeQuery(id+"F18.opPattern","COPY",EDGE,{"derivedFrom":makeQuery(id+"F17.opExtrude","CAP_EDGE",EDGE,{"disambiguationData":[OSD([sQuery(id+"F16.wireOp",EDGE,"E90")])],"isStart":false}),"instanceName":"1"});
            var Q4;
            Q4=makeQuery(id+"F17.opExtrude","SWEPT_EDGE",EDGE,{"disambiguationData":[OSD([sQuery(id+"F12.wireOp",EDGE,"E47.trimOffspring"),sQuery(id+"F16.wireOp",EDGE,"E90"),sQuery(id+"F16.wireOp",EDGE,"E91")])]});
            var Q5;
            Q5=makeQuery(id+"F18.opPattern","COPY",EDGE,{"derivedFrom":makeQuery(id+"F17.opExtrude","SWEPT_EDGE",EDGE,{"disambiguationData":[OSD([sQuery(id+"F12.wireOp",EDGE,"E47.trimOffspring"),sQuery(id+"F16.wireOp",EDGE,"E90"),sQuery(id+"F16.wireOp",EDGE,"E91")])]}),"instanceName":"1"});
            var Q6;
            Q6=makeQuery(id+"F13.opExtrude","CAP_EDGE",EDGE,{"disambiguationData":[OSD([sQuery(id+"F12.wireOp",EDGE,"E50.trimOffspring")])],"isStart":false});
            var Q7;
            Q7=makeQuery(id+"F13.opExtrude","CAP_EDGE",EDGE,{"disambiguationData":[OSD([sQuery(id+"F12.wireOp",EDGE,"E50.trimOffspring")])],"isStart":true});
            var Q8;
            Q8=makeQuery(id+"F13.opExtrude","SWEPT_EDGE",EDGE,{"disambiguationData":[OSD([sQuery(id+"F12.wireOp",EDGE,"E41"),sQuery(id+"F12.wireOp",EDGE,"E52.trimOffspring")])]});
            var Q9;
            Q9=makeQuery(id+"F13.opExtrude","CAP_EDGE",EDGE,{"disambiguationData":[OSD([sQuery(id+"F12.wireOp",EDGE,"E49.trimOffspring")])],"isStart":false});
            var Q10;
            Q10=makeQuery(id+"F13.opExtrude","CAP_EDGE",EDGE,{"disambiguationData":[OSD([sQuery(id+"F12.wireOp",EDGE,"E49.trimOffspring")])],"isStart":true});
            var Q11;
            Q11=makeQuery(id+"F13.opExtrude","CAP_EDGE",EDGE,{"disambiguationData":[OSD([sQuery(id+"F12.wireOp",EDGE,"E53.trimOffspring")])],"isStart":false});
            var Q12;
            Q12=makeQuery(id+"F13.opExtrude","CAP_EDGE",EDGE,{"disambiguationData":[OSD([sQuery(id+"F12.wireOp",EDGE,"E53.trimOffspring")])],"isStart":true});
            fillet(context, id + "F24", {"entities" : qUnion([Q0, Q1, Q2, Q3, Q4, Q5, Q6, Q7, Q8, Q9, Q10, Q11, Q12]), "radius" : 1.27 * mm, "tangentPropagation" : true, "allowEdgeOverflow" : false});
        }
        {
            var Q0;
            {var subQ0=makeQuery(id+"F17.opExtrude","SWEPT_EDGE",EDGE,{"disambiguationData":[OSD([sQuery(id+"F16.wireOp",EDGE,"E89"),sQuery(id+"F16.wireOp",EDGE,"E90")])]});Q0=makeQuery(id+"F19.opBoolean","MERGE",EDGE,{"derivedFrom":[makeQuery(id+"F13.opExtrude","SWEPT_EDGE",EDGE,{"disambiguationData":[OSD([sQuery(id+"F12.wireOp",EDGE,"E82"),sQuery(id+"F12.wireOp",EDGE,"E83")])]}),subQ0,makeQuery(id+"F18.opPattern","COPY",EDGE,{"derivedFrom":subQ0,"instanceName":"1"})]});}
            fillet(context, id + "F25", {"entities" : qUnion([Q0]), "radius" : 0.76 * mm, "tangentPropagation" : true, "allowEdgeOverflow" : false});
        }
        {
            var Q0;
            Q0=qCreatedBy(makeId("Front.planeOp"),FACE);
            cPlane(context, id + "F26", {"entities" : qUnion([Q0]), "cplaneType" : CPlaneType.OFFSET, "offset" : 88.9 * mm, "width" : 152.4 * mm, "height" : 152.4 * mm});
        }
        {
            var Q0;
            Q0=qCreatedBy(id+"F26.planeOp",FACE);
            cPlane(context, id + "F27", {"entities" : qUnion([Q0]), "cplaneType" : CPlaneType.OFFSET, "offset" : 177.8 * mm, "oppositeDirection" : true, "width" : 152.4 * mm, "height" : 152.4 * mm});
        }
        {
            var Q0;
            Q0=makeQuery(id+"F18.opPattern","COPY",BODY,{"derivedFrom":makeQuery(id+"F17.opExtrude","SWEPT_BODY",BODY,{"disambiguationData":[OSD([sQuery(id+"F16.wireOp",EDGE,"E89"),sQuery(id+"F16.wireOp",EDGE,"E90"),sQuery(id+"F16.wireOp",EDGE,"E91"),sQuery(id+"F16.wireOp",EDGE,"E92")])]}),"instanceName":"1"});
            var Q1;
            Q1=qCreatedBy(id+"F26.planeOp",FACE);
            mirror(context, id + "F28", {"entities" : qUnion([Q0]), "mirrorPlane" : qUnion([Q1])});
        }
        {
            var Q0;
            Q0=makeQuery(id+"F18.opPattern","COPY",BODY,{"derivedFrom":makeQuery(id+"F17.opExtrude","SWEPT_BODY",BODY,{"disambiguationData":[OSD([sQuery(id+"F16.wireOp",EDGE,"E89"),sQuery(id+"F16.wireOp",EDGE,"E90"),sQuery(id+"F16.wireOp",EDGE,"E91"),sQuery(id+"F16.wireOp",EDGE,"E92")])]}),"instanceName":"1"});
            var Q1;
            Q1=qCreatedBy(id+"F27.planeOp",FACE);
            mirror(context, id + "F29", {"entities" : qUnion([Q0]), "mirrorPlane" : qUnion([Q1])});
        }
        {
            var Q0;
            Q0=makeQuery(id+"F11.opExtrude","SWEPT_BODY",BODY,{"disambiguationData":[OSD([sQuery(id+"F10.wireOp",EDGE,"E35"),sQuery(id+"F10.wireOp",EDGE,"E36")])]});
            var Q1;
            Q1=makeQuery(id+"F28.opPattern","COPY",BODY,{"derivedFrom":makeQuery(id+"F18.opPattern","COPY",BODY,{"derivedFrom":makeQuery(id+"F17.opExtrude","SWEPT_BODY",BODY,{"disambiguationData":[OSD([sQuery(id+"F16.wireOp",EDGE,"E89"),sQuery(id+"F16.wireOp",EDGE,"E90"),sQuery(id+"F16.wireOp",EDGE,"E91"),sQuery(id+"F16.wireOp",EDGE,"E92")])]}),"instanceName":"1"}),"instanceName":"1"});
            var Q2;
            Q2=makeQuery(id+"F18.opPattern","COPY",BODY,{"derivedFrom":makeQuery(id+"F17.opExtrude","SWEPT_BODY",BODY,{"disambiguationData":[OSD([sQuery(id+"F16.wireOp",EDGE,"E89"),sQuery(id+"F16.wireOp",EDGE,"E90"),sQuery(id+"F16.wireOp",EDGE,"E91"),sQuery(id+"F16.wireOp",EDGE,"E92")])]}),"instanceName":"1"});
            var Q3;
            Q3=makeQuery(id+"F29.opPattern","COPY",BODY,{"derivedFrom":makeQuery(id+"F18.opPattern","COPY",BODY,{"derivedFrom":makeQuery(id+"F17.opExtrude","SWEPT_BODY",BODY,{"disambiguationData":[OSD([sQuery(id+"F16.wireOp",EDGE,"E89"),sQuery(id+"F16.wireOp",EDGE,"E90"),sQuery(id+"F16.wireOp",EDGE,"E91"),sQuery(id+"F16.wireOp",EDGE,"E92")])]}),"instanceName":"1"}),"instanceName":"1"});
            var Q4;
            Q4=qCreatedBy(makeId("Right.planeOp"),FACE);
            mirror(context, id + "F30", {"entities" : qUnion([Q0, Q1, Q2, Q3]), "mirrorPlane" : qUnion([Q4])});
        }
    });
